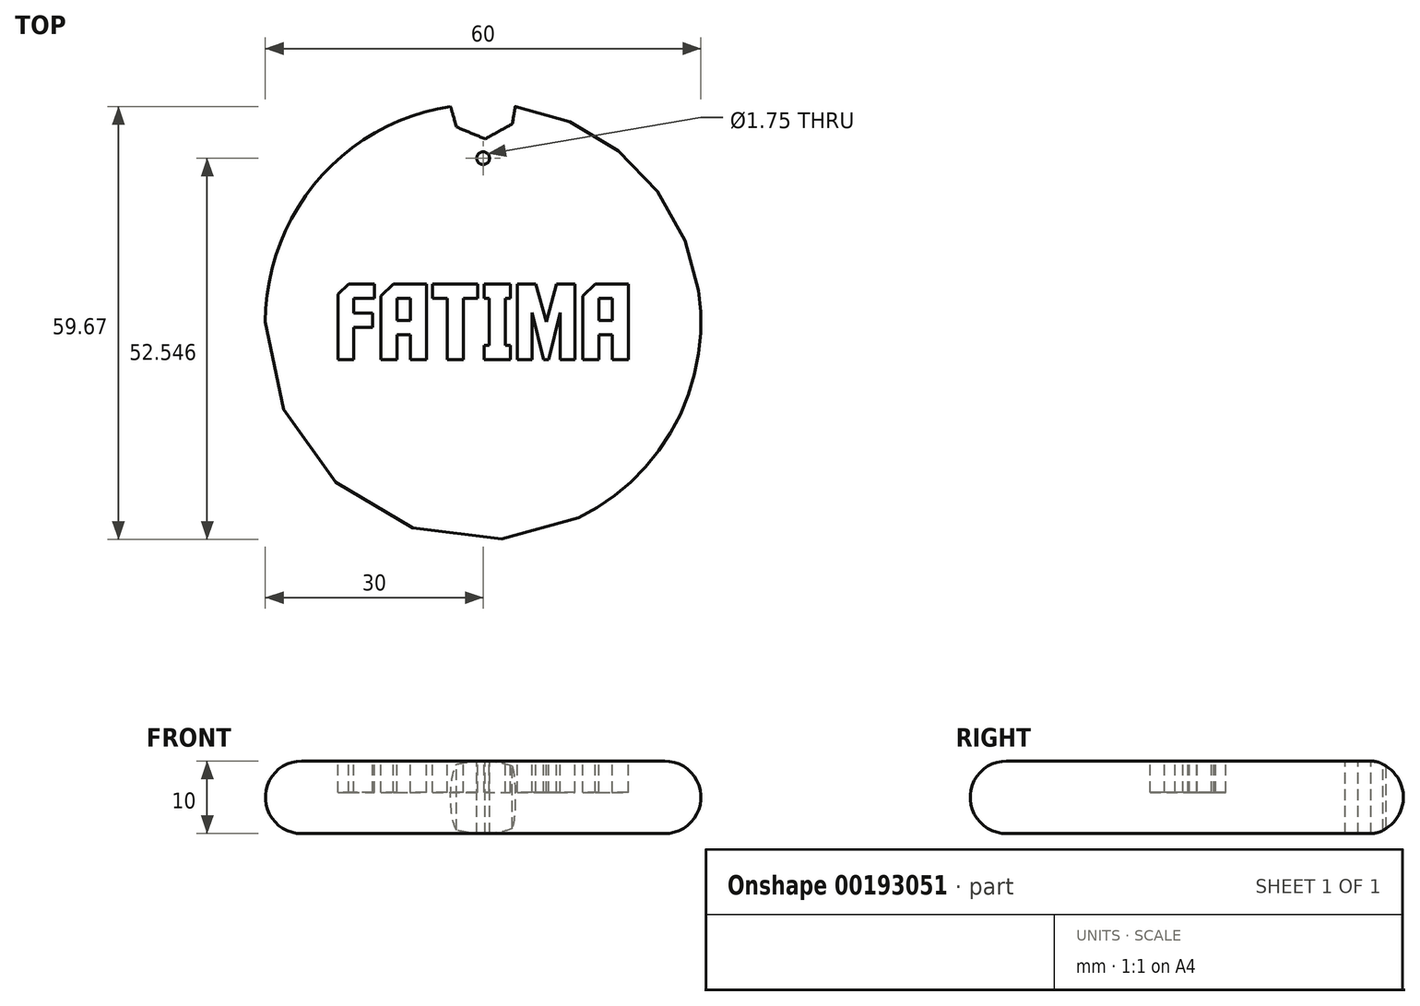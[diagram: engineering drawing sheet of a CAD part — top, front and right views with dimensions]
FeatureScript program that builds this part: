
annotation { "Feature Type Name" : "Feature", "Feature Type Description" : "" }
export const myFeature = defineFeature(function(context is Context, id is Id, definition is map)
    precondition{}
    {
        {
            var Q0;
            Q0=qCreatedBy(makeId("Front.planeOp"),FACE);
            var sketch = newSketch(context, id + "F0", { "sketchPlane" : qUnion([Q0])});
            skLineSegment(sketch, "E0.bottom", {"start": v(0, 0) * mm, "end": v(-25, 0) * mm});
            skLineSegment(sketch, "E0.top", {"start": v(0, 10) * mm, "end": v(-25, 10) * mm});
            skLineSegment(sketch, "E0.left", {"start": v(0, 0) * mm, "end": v(0, 10) * mm});
            skLineSegment(sketch, "E0.right", {"start": v(-25, 0) * mm, "end": v(-25, 10) * mm});
            skArc(sketch, "E1", {"start": v(-25, 10) * mm, "mid": v(-30, 5) * mm, "end": v(-25, 0) * mm});
            skSolve(sketch);
        }
        {
            var Q0;
            Q0 = qSketchRegion(id + "F0", true);
            var Q1;
            Q1=sQuery(id+"F0.wireOp",EDGE,"E0.left");
            revolve(context, id + "F1", {"entities" : qUnion([Q0]), "axis" : qUnion([Q1]), "revolveType" : RevolveType.FULL});
        }
        {
            var Q0;
            Q0=qCreatedBy(makeId("Top.planeOp"),FACE);
            cPlane(context, id + "F2", {"entities" : qUnion([Q0]), "cplaneType" : CPlaneType.OFFSET, "offset" : 10 * mm, "width" : 152.4 * mm, "height" : 152.4 * mm});
        }
        {
            var Q0;
            Q0=qCreatedBy(id+"F2.planeOp",FACE);
            var sketch = newSketch(context, id + "F3", { "sketchPlane" : qUnion([Q0])});
            skLineSegment(sketch, "E2", {"start": v(-17.8, -0.73) * mm, "end": v(-17.8, -5.23) * mm});
            skLineSegment(sketch, "E3", {"start": v(-17.8, -5.23) * mm, "end": v(-20, -5.23) * mm});
            skLineSegment(sketch, "E4", {"start": v(-20, -5.23) * mm, "end": v(-20, 3.79) * mm});
            skLineSegment(sketch, "E5", {"start": v(-20, 3.79) * mm, "end": v(-18.55, 5.23) * mm});
            skLineSegment(sketch, "E6", {"start": v(-18.55, 5.23) * mm, "end": v(-15, 5.23) * mm});
            skLineSegment(sketch, "E7", {"start": v(-15, 5.23) * mm, "end": v(-15, 3.24) * mm});
            skLineSegment(sketch, "E8", {"start": v(-15, 3.24) * mm, "end": v(-17.8, 3.24) * mm});
            skLineSegment(sketch, "E9", {"start": v(-17.8, 3.24) * mm, "end": v(-17.8, 1.22) * mm});
            skLineSegment(sketch, "E10", {"start": v(-17.8, 1.22) * mm, "end": v(-15.22, 1.22) * mm});
            skLineSegment(sketch, "E11", {"start": v(-15.22, 1.22) * mm, "end": v(-15.22, -0.73) * mm});
            skLineSegment(sketch, "E12", {"start": v(-15.22, -0.73) * mm, "end": v(-17.8, -0.73) * mm});
            skLineSegment(sketch, "E13", {"start": v(-11.89, -5.23) * mm, "end": v(-14.09, -5.23) * mm});
            skLineSegment(sketch, "E14", {"start": v(-14.09, -5.23) * mm, "end": v(-14.09, 3.58) * mm});
            skLineSegment(sketch, "E15", {"start": v(-14.09, 3.58) * mm, "end": v(-12.4, 5.23) * mm});
            skLineSegment(sketch, "E16", {"start": v(-12.4, 5.23) * mm, "end": v(-7.83, 5.23) * mm});
            skLineSegment(sketch, "E17", {"start": v(-7.83, 5.23) * mm, "end": v(-7.83, -5.23) * mm});
            skLineSegment(sketch, "E18", {"start": v(-7.83, -5.23) * mm, "end": v(-10.02, -5.23) * mm});
            skLineSegment(sketch, "E19", {"start": v(-10.02, -5.23) * mm, "end": v(-10.02, -1.8) * mm});
            skLineSegment(sketch, "E20", {"start": v(-10.02, -1.8) * mm, "end": v(-11.89, -1.8) * mm});
            skLineSegment(sketch, "E21", {"start": v(-11.89, -1.8) * mm, "end": v(-11.89, -5.23) * mm});
            skLineSegment(sketch, "E22", {"start": v(-10.02, 0.2) * mm, "end": v(-10.02, 3.24) * mm});
            skLineSegment(sketch, "E23", {"start": v(-10.02, 3.24) * mm, "end": v(-11.89, 3.24) * mm});
            skLineSegment(sketch, "E24", {"start": v(-11.89, 3.24) * mm, "end": v(-11.89, 0.2) * mm});
            skLineSegment(sketch, "E25", {"start": v(-11.89, 0.2) * mm, "end": v(-10.02, 0.2) * mm});
            skLineSegment(sketch, "E26", {"start": v(-0.77, 3.24) * mm, "end": v(-2.75, 3.24) * mm});
            skLineSegment(sketch, "E27", {"start": v(-2.75, 3.24) * mm, "end": v(-2.75, -5.23) * mm});
            skLineSegment(sketch, "E28", {"start": v(-2.75, -5.23) * mm, "end": v(-4.95, -5.23) * mm});
            skLineSegment(sketch, "E29", {"start": v(-4.95, -5.23) * mm, "end": v(-4.95, 3.24) * mm});
            skLineSegment(sketch, "E30", {"start": v(-4.95, 3.24) * mm, "end": v(-7, 3.24) * mm});
            skLineSegment(sketch, "E31", {"start": v(-7, 3.24) * mm, "end": v(-7, 5.23) * mm});
            skLineSegment(sketch, "E32", {"start": v(-7, 5.23) * mm, "end": v(-0.77, 5.23) * mm});
            skLineSegment(sketch, "E33", {"start": v(-0.77, 5.23) * mm, "end": v(-0.77, 3.24) * mm});
            skLineSegment(sketch, "E34", {"start": v(3.76, -3.25) * mm, "end": v(3.76, -5.23) * mm});
            skLineSegment(sketch, "E35", {"start": v(3.76, -5.23) * mm, "end": v(0.12, -5.23) * mm});
            skLineSegment(sketch, "E36", {"start": v(0.12, -5.23) * mm, "end": v(0.12, -3.25) * mm});
            skLineSegment(sketch, "E37", {"start": v(0.12, -3.25) * mm, "end": v(0.84, -3.25) * mm});
            skLineSegment(sketch, "E38", {"start": v(0.84, -3.25) * mm, "end": v(0.84, 3.25) * mm});
            skLineSegment(sketch, "E39", {"start": v(0.84, 3.25) * mm, "end": v(0.12, 3.25) * mm});
            skLineSegment(sketch, "E40", {"start": v(0.12, 3.25) * mm, "end": v(0.12, 5.23) * mm});
            skLineSegment(sketch, "E41", {"start": v(0.12, 5.23) * mm, "end": v(3.76, 5.23) * mm});
            skLineSegment(sketch, "E42", {"start": v(3.76, 5.23) * mm, "end": v(3.76, 3.25) * mm});
            skLineSegment(sketch, "E43", {"start": v(3.76, 3.25) * mm, "end": v(3.04, 3.25) * mm});
            skLineSegment(sketch, "E44", {"start": v(3.04, 3.25) * mm, "end": v(3.04, -3.25) * mm});
            skLineSegment(sketch, "E45", {"start": v(3.04, -3.25) * mm, "end": v(3.76, -3.25) * mm});
            skLineSegment(sketch, "E46", {"start": v(10.13, 5.23) * mm, "end": v(12.66, 5.23) * mm});
            skLineSegment(sketch, "E47", {"start": v(12.66, 5.23) * mm, "end": v(12.66, -5.23) * mm});
            skLineSegment(sketch, "E48", {"start": v(12.66, -5.23) * mm, "end": v(10.64, -5.23) * mm});
            skLineSegment(sketch, "E49", {"start": v(10.64, -5.23) * mm, "end": v(10.64, 1.28) * mm});
            skLineSegment(sketch, "E50", {"start": v(10.64, 1.28) * mm, "end": v(9, -5.23) * mm});
            skLineSegment(sketch, "E51", {"start": v(9, -5.23) * mm, "end": v(8.36, -5.23) * mm});
            skLineSegment(sketch, "E52", {"start": v(8.36, -5.23) * mm, "end": v(6.73, 1.28) * mm});
            skLineSegment(sketch, "E53", {"start": v(6.73, 1.28) * mm, "end": v(6.73, -5.23) * mm});
            skLineSegment(sketch, "E54", {"start": v(6.73, -5.23) * mm, "end": v(4.7, -5.23) * mm});
            skLineSegment(sketch, "E55", {"start": v(4.7, -5.23) * mm, "end": v(4.7, 5.23) * mm});
            skLineSegment(sketch, "E56", {"start": v(4.7, 5.23) * mm, "end": v(7.23, 5.23) * mm});
            skLineSegment(sketch, "E57", {"start": v(7.23, 5.23) * mm, "end": v(8.68, 0.02) * mm});
            skLineSegment(sketch, "E58", {"start": v(8.68, 0.02) * mm, "end": v(10.13, 5.23) * mm});
            skLineSegment(sketch, "E59", {"start": v(15.94, -5.23) * mm, "end": v(13.74, -5.23) * mm});
            skLineSegment(sketch, "E60", {"start": v(13.74, -5.23) * mm, "end": v(13.74, 3.58) * mm});
            skLineSegment(sketch, "E61", {"start": v(13.74, 3.58) * mm, "end": v(15.43, 5.23) * mm});
            skLineSegment(sketch, "E62", {"start": v(15.43, 5.23) * mm, "end": v(20, 5.23) * mm});
            skLineSegment(sketch, "E63", {"start": v(20, 5.23) * mm, "end": v(20, -5.23) * mm});
            skLineSegment(sketch, "E64", {"start": v(20, -5.23) * mm, "end": v(17.8, -5.23) * mm});
            skLineSegment(sketch, "E65", {"start": v(17.8, -5.23) * mm, "end": v(17.8, -1.8) * mm});
            skLineSegment(sketch, "E66", {"start": v(17.8, -1.8) * mm, "end": v(15.94, -1.8) * mm});
            skLineSegment(sketch, "E67", {"start": v(15.94, -1.8) * mm, "end": v(15.94, -5.23) * mm});
            skLineSegment(sketch, "E68", {"start": v(17.8, 0.2) * mm, "end": v(17.8, 3.24) * mm});
            skLineSegment(sketch, "E69", {"start": v(17.8, 3.24) * mm, "end": v(15.94, 3.24) * mm});
            skLineSegment(sketch, "E70", {"start": v(15.94, 3.24) * mm, "end": v(15.94, 0.2) * mm});
            skLineSegment(sketch, "E71", {"start": v(15.94, 0.2) * mm, "end": v(17.8, 0.2) * mm});
            skSolve(sketch);
        }
        {
            var Q0;
            Q0=makeQuery(id+"F3.imprint","IMPRINT",FACE,{"disambiguationData":[TD([[makeQuery(id+"F3.imprint","IMPRINT",EDGE,{"derivedFrom":sQuery(id+"F3.wireOp",EDGE,"E2")}),-1.0]])]});
            var Q1;
            Q1=makeQuery(id+"F3.imprint","IMPRINT",FACE,{"disambiguationData":[TD([[makeQuery(id+"F3.imprint","IMPRINT",EDGE,{"derivedFrom":sQuery(id+"F3.wireOp",EDGE,"E13")}),-1.0]])]});
            var Q2;
            Q2=makeQuery(id+"F3.imprint","IMPRINT",FACE,{"disambiguationData":[TD([[makeQuery(id+"F3.imprint","IMPRINT",EDGE,{"derivedFrom":sQuery(id+"F3.wireOp",EDGE,"E26")}),-1.0]])]});
            var Q3;
            Q3=makeQuery(id+"F3.imprint","IMPRINT",FACE,{"disambiguationData":[TD([[makeQuery(id+"F3.imprint","IMPRINT",EDGE,{"derivedFrom":sQuery(id+"F3.wireOp",EDGE,"E34")}),-1.0]])]});
            var Q4;
            Q4=makeQuery(id+"F3.imprint","IMPRINT",FACE,{"disambiguationData":[TD([[makeQuery(id+"F3.imprint","IMPRINT",EDGE,{"derivedFrom":sQuery(id+"F3.wireOp",EDGE,"E46")}),-1.0]])]});
            var Q5;
            Q5=makeQuery(id+"F3.imprint","IMPRINT",FACE,{"disambiguationData":[TD([[makeQuery(id+"F3.imprint","IMPRINT",EDGE,{"derivedFrom":sQuery(id+"F3.wireOp",EDGE,"E59")}),-1.0]])]});
            extrude(context, id + "F4", {"entities" : qUnion([Q0, Q1, Q2, Q3, Q4, Q5]), "operationType" : NewBodyOperationType.REMOVE, "oppositeDirection" : true, "depth" : 4.3 * mm});
        }
        {
            var Q0;
            Q0=qCreatedBy(id+"F2.planeOp",FACE);
            var sketch = newSketch(context, id + "F5", { "sketchPlane" : qUnion([Q0])});
            skCircle(sketch, "E72.cCircle", {"center": v(0, 30.13) * mm, "radius": 4.44 * mm, "construction": true});
            skLineSegment(sketch, "E72.0", {"start": v(4.02, 27.28) * mm, "end": v(0.28, 25.21) * mm});
            skLineSegment(sketch, "E72.1", {"start": v(0.28, 25.21) * mm, "end": v(-3.67, 26.85) * mm});
            skLineSegment(sketch, "E72.2", {"start": v(-3.67, 26.85) * mm, "end": v(-4.85, 30.95) * mm});
            skLineSegment(sketch, "E72.3", {"start": v(-4.85, 30.95) * mm, "end": v(-2.38, 34.44) * mm});
            skLineSegment(sketch, "E72.4", {"start": v(-2.38, 34.44) * mm, "end": v(1.88, 34.68) * mm});
            skLineSegment(sketch, "E72.5", {"start": v(1.88, 34.68) * mm, "end": v(4.73, 31.5) * mm});
            skLineSegment(sketch, "E72.6", {"start": v(4.73, 31.5) * mm, "end": v(4.02, 27.28) * mm});
            skPoint(sketch, "E72.0.midPoint", {"position": v(2.15, 26.24) * mm});
            skSolve(sketch);
        }
        {
            var Q0;
            Q0=makeQuery(id+"F5.imprint","IMPRINT",FACE,{"disambiguationData":[TD([[makeQuery(id+"F5.imprint","IMPRINT",EDGE,{"derivedFrom":sQuery(id+"F5.wireOp",EDGE,"E72.0")}),-1.0]])]});
            extrude(context, id + "F6", {"entities" : qUnion([Q0]), "operationType" : NewBodyOperationType.REMOVE, "oppositeDirection" : true, "depth" : 25.4 * mm});
        }
        {
            var Q0;
            Q0=qCreatedBy(id+"F2.planeOp",FACE);
            var sketch = newSketch(context, id + "F7", { "sketchPlane" : qUnion([Q0])});
            skCircle(sketch, "E73", {"center": v(0, 22.55) * mm, "radius": 0.88 * mm});
            skSolve(sketch);
        }
        {
            var Q0;
            Q0=makeQuery(id+"F7.imprint","IMPRINT",FACE,{"disambiguationData":[TD([[makeQuery(id+"F7.imprint","IMPRINT",EDGE,{"derivedFrom":sQuery(id+"F7.wireOp",EDGE,"E73")}),1.0]])]});
            extrude(context, id + "F8", {"entities" : qUnion([Q0]), "operationType" : NewBodyOperationType.REMOVE, "oppositeDirection" : true, "depth" : 25.4 * mm});
        }
    });
